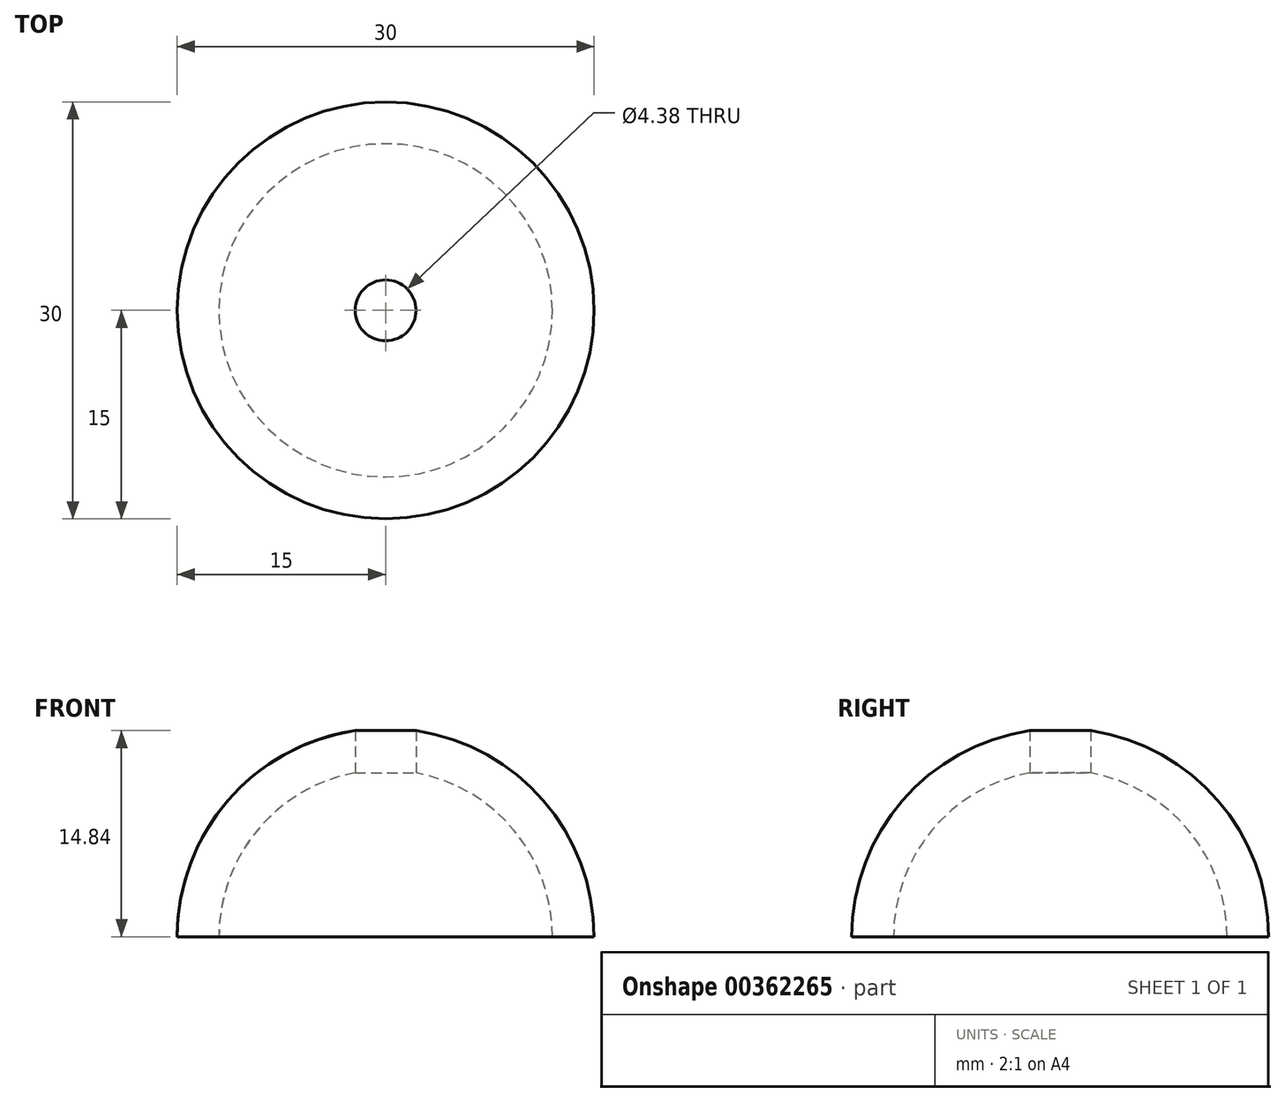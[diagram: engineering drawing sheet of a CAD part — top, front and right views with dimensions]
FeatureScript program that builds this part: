
annotation { "Feature Type Name" : "Feature", "Feature Type Description" : "" }
export const myFeature = defineFeature(function(context is Context, id is Id, definition is map)
    precondition{}
    {
        {
            var Q0;
            Q0=qCreatedBy(makeId("Front.planeOp"),FACE);
            var sketch = newSketch(context, id + "F0", { "sketchPlane" : qUnion([Q0])});
            skLineSegment(sketch, "E0", {"start": v(0, 0) * mm, "end": v(0, 15) * mm});
            skLineSegment(sketch, "E1", {"start": v(0, 0) * mm, "end": v(15, 0) * mm});
            skArc(sketch, "E2", {"start": v(15, 0) * mm, "mid": v(10.6, 10.6) * mm, "end": v(0, 15) * mm});
            skSolve(sketch);
        }
        {
            var Q0;
            Q0=qSketchRegion(id+"F0",true);
            var Q1;
            Q1=sQuery(id+"F0.wireOp",EDGE,"E0");
            revolve(context, id + "F1", {"entities" : qUnion([Q0]), "axis" : qUnion([Q1]), "revolveType" : RevolveType.FULL});
        }
        {
            var Q0;
            Q0=makeQuery(id+"F1.opRevolve","SWEPT_FACE",FACE,{"disambiguationData":[OSD([sQuery(id+"F0.wireOp",EDGE,"E1")])]});
            shell(context, id + "F2", {"entities" : qUnion([Q0]), "thickness" : 3 * mm});
        }
        {
            var Q0;
            Q0=qCreatedBy(makeId("Top.planeOp"),FACE);
            var sketch = newSketch(context, id + "F3", { "sketchPlane" : qUnion([Q0])});
            skCircle(sketch, "E3", {"center": v(0, 0) * mm, "radius": 2.2 * mm});
            skSolve(sketch);
        }
        {
            var Q0;
            Q0 = qSketchRegion(id + "F3", true);
            extrude(context, id + "F4", {"entities" : qUnion([Q0]), "operationType" : NewBodyOperationType.REMOVE, "depth" : 25 * mm});
        }
    });
